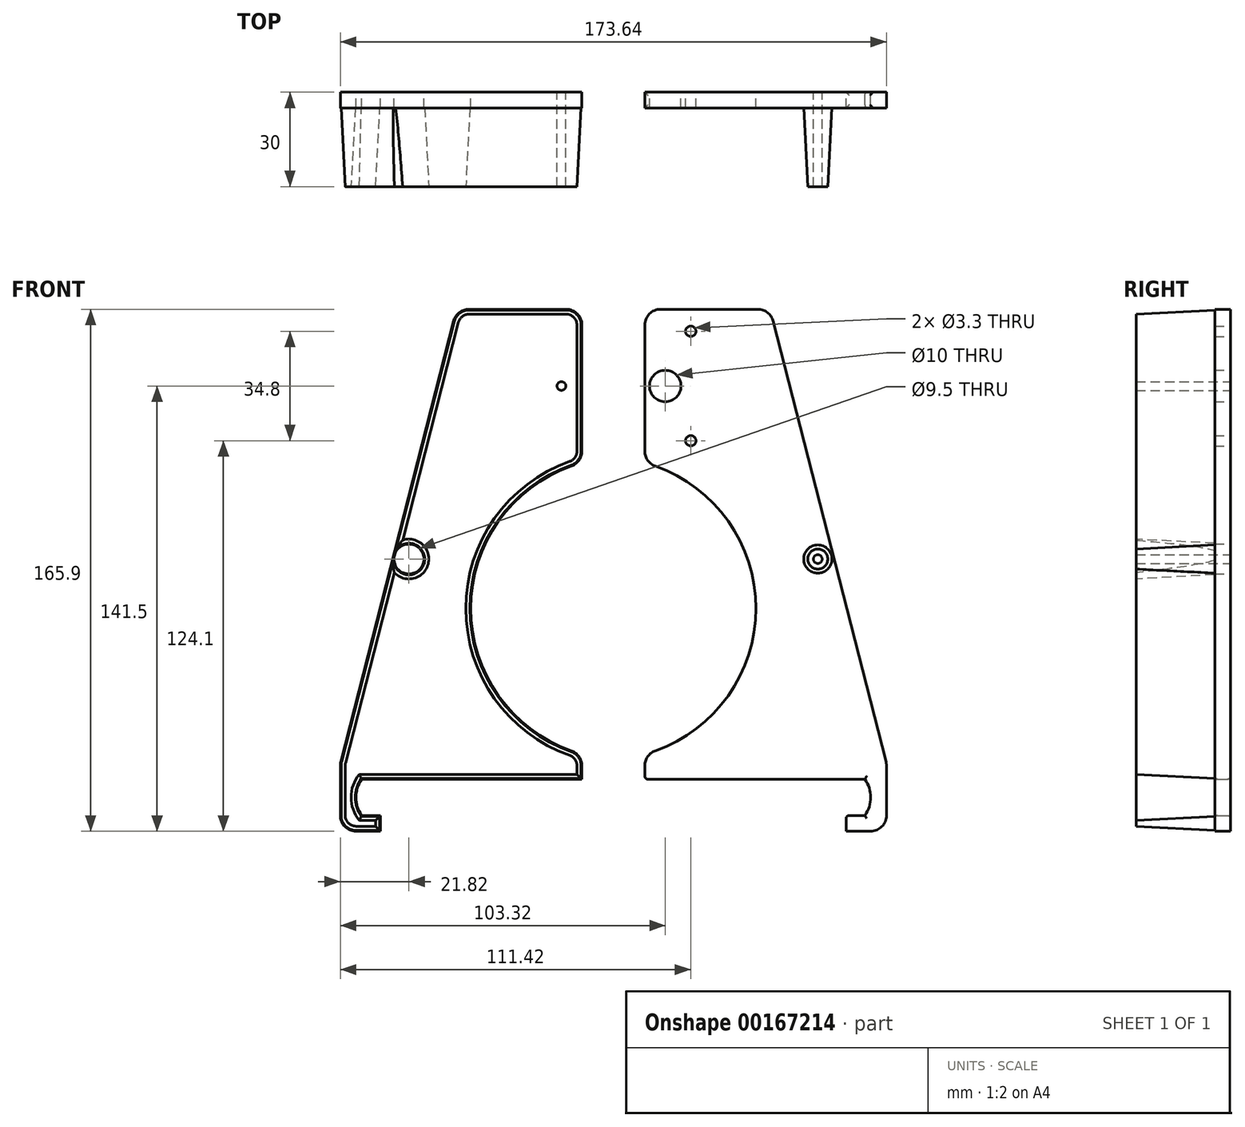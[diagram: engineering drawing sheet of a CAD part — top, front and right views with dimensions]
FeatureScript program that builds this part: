
annotation { "Feature Type Name" : "Feature", "Feature Type Description" : "" }
export const myFeature = defineFeature(function(context is Context, id is Id, definition is map)
    precondition{}
    {
        {
            var Q0;
            Q0=qCreatedBy(makeId("Front.planeOp"),FACE);
            var sketch = newSketch(context, id + "F0", { "sketchPlane" : qUnion([Q0])});
            skLineSegment(sketch, "E0", {"start": v(0, 0) * mm, "end": v(70, 0) * mm});
            skLineSegment(sketch, "E1", {"start": v(70, -11.5) * mm, "end": v(64, -11.5) * mm});
            skLineSegment(sketch, "E2", {"start": v(64, -11.5) * mm, "end": v(64, -16.5) * mm});
            skLineSegment(sketch, "E3", {"start": v(64, -16.5) * mm, "end": v(71.82, -16.5) * mm});
            skLineSegment(sketch, "E4", {"start": v(76.82, -11.5) * mm, "end": v(76.82, 4.37) * mm});
            skLineSegment(sketch, "E5", {"start": v(76.66, 5.61) * mm, "end": v(40.78, 145.64) * mm});
            skLineSegment(sketch, "E6", {"start": v(35.93, 149.4) * mm, "end": v(5, 149.4) * mm});
            skLineSegment(sketch, "E7", {"start": v(0, 144.4) * mm, "end": v(0, 104.27) * mm});
            skArc(sketch, "E8", {"start": v(70, 0) * mm, "mid": v(71.82, -5.75) * mm, "end": v(70, -11.5) * mm});
            skPoint(sketch, "E9", {"position": v(55, 70) * mm});
            skPoint(sketch, "E10", {"position": v(6.5, 125) * mm});
            skPoint(sketch, "E11", {"position": v(14.6, 142.4) * mm});
            skPoint(sketch, "E12", {"position": v(14.6, 107.6) * mm});
            skLineSegment(sketch, "E13", {"start": v(0, 0) * mm, "end": v(0, 4.33) * mm});
            skArc(sketch, "E14", {"start": v(3.33, 9.04) * mm, "mid": v(35.34, 54.3) * mm, "end": v(3.33, 99.56) * mm});
            skCircle(sketch, "E15", {"center": v(55, 70) * mm, "radius": 4.75 * mm});
            skLineSegment(sketch, "E16", {"start": v(-10, 173.2) * mm, "end": v(-10, -16.35) * mm, "construction": true});
            skPoint(sketch, "E17.visualSharp", {"position": v(39.81, 149.4) * mm});
            skArc(sketch, "E17.filletArc", {"start": v(40.78, 145.64) * mm, "mid": v(39, 148.35) * mm, "end": v(35.93, 149.4) * mm});
            skPoint(sketch, "E18.visualSharp", {"position": v(0, 149.4) * mm});
            skArc(sketch, "E18.filletArc", {"start": v(5, 149.4) * mm, "mid": v(1.46, 147.94) * mm, "end": v(0, 144.4) * mm});
            skPoint(sketch, "E19.visualSharp", {"position": v(0, 100.6) * mm});
            skArc(sketch, "E19.filletArc", {"start": v(0, 104.27) * mm, "mid": v(0.92, 101.38) * mm, "end": v(3.33, 99.56) * mm});
            skPoint(sketch, "E20.visualSharp", {"position": v(0, 8) * mm});
            skArc(sketch, "E20.filletArc", {"start": v(3.33, 9.04) * mm, "mid": v(0.92, 7.22) * mm, "end": v(0, 4.33) * mm});
            skPoint(sketch, "E21.visualSharp", {"position": v(76.82, -16.5) * mm});
            skArc(sketch, "E21.filletArc", {"start": v(71.82, -16.5) * mm, "mid": v(75.35, -15.04) * mm, "end": v(76.82, -11.5) * mm});
            skPoint(sketch, "E22.visualSharp", {"position": v(76.82, 5) * mm});
            skArc(sketch, "E22.filletArc", {"start": v(76.82, 4.37) * mm, "mid": v(76.78, 5) * mm, "end": v(76.66, 5.61) * mm});
            skLineSegment(sketch, "E23.MirrorCS", {"start": v(-20, 144.4) * mm, "end": v(-20, 104.27) * mm});
            skPoint(sketch, "E24.MirrorP", {"position": v(-96.82, 5) * mm});
            skLineSegment(sketch, "E25.MirrorCS", {"start": v(-96.82, -11.5) * mm, "end": v(-96.82, 4.37) * mm});
            skLineSegment(sketch, "E26.MirrorCS", {"start": v(-84, -16.5) * mm, "end": v(-91.82, -16.5) * mm});
            skPoint(sketch, "E27.MirrorP", {"position": v(-20, 100.6) * mm});
            skLineSegment(sketch, "E28.MirrorCS", {"start": v(-84, -11.5) * mm, "end": v(-84, -16.5) * mm});
            skPoint(sketch, "E29.MirrorP", {"position": v(-59.81, 149.4) * mm});
            skPoint(sketch, "E30.MirrorP", {"position": v(-34.6, 142.4) * mm});
            skLineSegment(sketch, "E31.MirrorCS", {"start": v(-90, -11.5) * mm, "end": v(-84, -11.5) * mm});
            skArc(sketch, "E32.MirrorCS", {"start": v(-23.33, 9.04) * mm, "mid": v(-20.92, 7.22) * mm, "end": v(-20, 4.33) * mm});
            skPoint(sketch, "E33.MirrorP", {"position": v(-96.82, -16.5) * mm});
            skCircle(sketch, "E34.MirrorC", {"center": v(-75, 70) * mm, "radius": 4.75 * mm});
            skLineSegment(sketch, "E35.MirrorCS", {"start": v(-20, 0) * mm, "end": v(-90, 0) * mm});
            skArc(sketch, "E36.MirrorCS", {"start": v(-20, 104.27) * mm, "mid": v(-20.92, 101.38) * mm, "end": v(-23.33, 99.56) * mm});
            skPoint(sketch, "E37.MirrorP", {"position": v(-34.6, 107.6) * mm});
            skArc(sketch, "E38.MirrorCS", {"start": v(-23.33, 9.04) * mm, "mid": v(-55.34, 54.3) * mm, "end": v(-23.33, 99.56) * mm});
            skArc(sketch, "E39.MirrorCS", {"start": v(-25, 149.4) * mm, "mid": v(-21.46, 147.94) * mm, "end": v(-20, 144.4) * mm});
            skArc(sketch, "E40.MirrorCS", {"start": v(-91.82, -16.5) * mm, "mid": v(-95.35, -15.04) * mm, "end": v(-96.82, -11.5) * mm});
            skLineSegment(sketch, "E41.MirrorCS", {"start": v(-20, 0) * mm, "end": v(-20, 4.33) * mm});
            skPoint(sketch, "E42.MirrorP", {"position": v(-20, 149.4) * mm});
            skArc(sketch, "E43.MirrorCS", {"start": v(-60.78, 145.64) * mm, "mid": v(-59, 148.35) * mm, "end": v(-55.93, 149.4) * mm});
            skLineSegment(sketch, "E44.MirrorCS", {"start": v(-55.93, 149.4) * mm, "end": v(-25, 149.4) * mm});
            skPoint(sketch, "E45.MirrorP", {"position": v(-26.5, 125) * mm});
            skArc(sketch, "E46.MirrorCS", {"start": v(-90, 0) * mm, "mid": v(-91.82, -5.75) * mm, "end": v(-90, -11.5) * mm});
            skLineSegment(sketch, "E47.MirrorCS", {"start": v(-96.66, 5.61) * mm, "end": v(-60.78, 145.64) * mm});
            skArc(sketch, "E48.MirrorCS", {"start": v(-96.82, 4.37) * mm, "mid": v(-96.78, 5) * mm, "end": v(-96.66, 5.61) * mm});
            skPoint(sketch, "E49.MirrorP", {"position": v(-20, 8) * mm});
            skSolve(sketch);
        }
        {
            var Q0;
            Q0=makeQuery(id+"F0.imprint","IMPRINT",FACE,{"disambiguationData":[TD([[makeQuery(id+"F0.imprint","IMPRINT",EDGE,{"derivedFrom":sQuery(id+"F0.wireOp",EDGE,"E0")}),1.0]])]});
            var Q1;
            Q1=makeQuery(id+"F0.imprint","IMPRINT",FACE,{"disambiguationData":[TD([[makeQuery(id+"F0.imprint","IMPRINT",EDGE,{"derivedFrom":sQuery(id+"F0.wireOp",EDGE,"E23.MirrorCS")}),-1.0]])]});
            var Q2;
            Q2=makeQuery(id+"F0.imprint","IMPRINT",FACE,{"disambiguationData":[TD([[makeQuery(id+"F0.imprint","IMPRINT",EDGE,{"derivedFrom":sQuery(id+"F0.wireOp",EDGE,"E15")}),1.0]])]});
            var Q3;
            Q3=makeQuery(id+"F0.imprint","IMPRINT",FACE,{"disambiguationData":[TD([[makeQuery(id+"F0.imprint","IMPRINT",EDGE,{"derivedFrom":sQuery(id+"F0.wireOp",EDGE,"E34.MirrorC")}),-1.0]])]});
            extrude(context, id + "F1", {"entities" : qUnion([Q0, Q1, Q2, Q3]), "depth" : 5 * mm});
        }
        {
            var Q0;
            Q0=makeQuery(id+"F0.imprint","IMPRINT",FACE,{"disambiguationData":[TD([[makeQuery(id+"F0.imprint","IMPRINT",EDGE,{"derivedFrom":sQuery(id+"F0.wireOp",EDGE,"E15")}),1.0]])]});
            var Q1;
            Q1=makeQuery(id+"F0.imprint","IMPRINT",FACE,{"disambiguationData":[TD([[makeQuery(id+"F0.imprint","IMPRINT",EDGE,{"derivedFrom":sQuery(id+"F0.wireOp",EDGE,"E34.MirrorC")}),-1.0]])]});
            extrude(context, id + "F2", {"entities" : qUnion([Q0, Q1]), "operationType" : NewBodyOperationType.ADD, "depth" : 30 * mm, "hasDraft" : true, "draftAngle" : 3 * degree, "draftPullDirection" : true});
        }
        {
            var Q0;
            Q0=sQuery(id+"F0.wireOp",VERTEX,"E11");
            var Q1;
            Q1=sQuery(id+"F0.wireOp",VERTEX,"E12");
            var Q2;
            Q2=makeQuery(id+"F1.opExtrude","SWEPT_BODY",BODY,{"disambiguationData":[OSD([sQuery(id+"F0.wireOp",EDGE,"E23.MirrorCS"),sQuery(id+"F0.wireOp",EDGE,"E25.MirrorCS"),sQuery(id+"F0.wireOp",EDGE,"E26.MirrorCS"),sQuery(id+"F0.wireOp",EDGE,"E28.MirrorCS"),sQuery(id+"F0.wireOp",EDGE,"E31.MirrorCS"),sQuery(id+"F0.wireOp",EDGE,"E32.MirrorCS"),sQuery(id+"F0.wireOp",EDGE,"E34.MirrorC"),sQuery(id+"F0.wireOp",EDGE,"E35.MirrorCS"),sQuery(id+"F0.wireOp",EDGE,"E36.MirrorCS"),sQuery(id+"F0.wireOp",EDGE,"E38.MirrorCS"),sQuery(id+"F0.wireOp",EDGE,"E39.MirrorCS"),sQuery(id+"F0.wireOp",EDGE,"E40.MirrorCS"),sQuery(id+"F0.wireOp",EDGE,"E41.MirrorCS"),sQuery(id+"F0.wireOp",EDGE,"E43.MirrorCS"),sQuery(id+"F0.wireOp",EDGE,"E44.MirrorCS"),sQuery(id+"F0.wireOp",EDGE,"E46.MirrorCS"),sQuery(id+"F0.wireOp",EDGE,"E47.MirrorCS"),sQuery(id+"F0.wireOp",EDGE,"E48.MirrorCS")])]});
            var Q3;
            Q3=makeQuery(id+"F1.opExtrude","SWEPT_BODY",BODY,{"disambiguationData":[OSD([sQuery(id+"F0.wireOp",EDGE,"E0"),sQuery(id+"F0.wireOp",EDGE,"E1"),sQuery(id+"F0.wireOp",EDGE,"E2"),sQuery(id+"F0.wireOp",EDGE,"E3"),sQuery(id+"F0.wireOp",EDGE,"E4"),sQuery(id+"F0.wireOp",EDGE,"E5"),sQuery(id+"F0.wireOp",EDGE,"E6"),sQuery(id+"F0.wireOp",EDGE,"E7"),sQuery(id+"F0.wireOp",EDGE,"E8"),sQuery(id+"F0.wireOp",EDGE,"E13"),sQuery(id+"F0.wireOp",EDGE,"E14"),sQuery(id+"F0.wireOp",EDGE,"E15"),sQuery(id+"F0.wireOp",EDGE,"E17.filletArc"),sQuery(id+"F0.wireOp",EDGE,"E18.filletArc"),sQuery(id+"F0.wireOp",EDGE,"E19.filletArc"),sQuery(id+"F0.wireOp",EDGE,"E20.filletArc"),sQuery(id+"F0.wireOp",EDGE,"E21.filletArc"),sQuery(id+"F0.wireOp",EDGE,"E22.filletArc")])]});
            hole(context, id + "F3", {"style" : HoleStyle.SIMPLE, "endStyle" : HoleEndStyle.THROUGH, "oppositeDirection" : true, "standardTappedOrClearance" : lookupTablePath({ "standard" : "ISO", "fit" : "Normal", "size" : "M3", "type" : "Clearance" }), "standardBlindInLast" : lookupTablePath({ "fit" : "Standard", "standard" : "ISO", "size" : "M3", "type" : "Clearance" }), "holeDiameter" : 3.3 * mm, "locations" : qUnion([Q0, Q1]), "scope" : qUnion([Q2, Q3]), "isTappedThrough" : true});
        }
        {
            var Q0;
            Q0=sQuery(id+"F0.wireOp",VERTEX,"E34.MirrorC.center");
            var Q1;
            Q1=sQuery(id+"F0.wireOp",VERTEX,"E45.MirrorP");
            var Q2;
            Q2=sQuery(id+"F0.wireOp",VERTEX,"E9");
            var Q3;
            Q3=makeQuery(id+"F1.opExtrude","SWEPT_BODY",BODY,{"disambiguationData":[OSD([sQuery(id+"F0.wireOp",EDGE,"E23.MirrorCS"),sQuery(id+"F0.wireOp",EDGE,"E25.MirrorCS"),sQuery(id+"F0.wireOp",EDGE,"E26.MirrorCS"),sQuery(id+"F0.wireOp",EDGE,"E28.MirrorCS"),sQuery(id+"F0.wireOp",EDGE,"E31.MirrorCS"),sQuery(id+"F0.wireOp",EDGE,"E32.MirrorCS"),sQuery(id+"F0.wireOp",EDGE,"E34.MirrorC"),sQuery(id+"F0.wireOp",EDGE,"E35.MirrorCS"),sQuery(id+"F0.wireOp",EDGE,"E36.MirrorCS"),sQuery(id+"F0.wireOp",EDGE,"E38.MirrorCS"),sQuery(id+"F0.wireOp",EDGE,"E39.MirrorCS"),sQuery(id+"F0.wireOp",EDGE,"E40.MirrorCS"),sQuery(id+"F0.wireOp",EDGE,"E41.MirrorCS"),sQuery(id+"F0.wireOp",EDGE,"E43.MirrorCS"),sQuery(id+"F0.wireOp",EDGE,"E44.MirrorCS"),sQuery(id+"F0.wireOp",EDGE,"E46.MirrorCS"),sQuery(id+"F0.wireOp",EDGE,"E47.MirrorCS"),sQuery(id+"F0.wireOp",EDGE,"E48.MirrorCS")])]});
            var Q4;
            Q4=makeQuery(id+"F1.opExtrude","SWEPT_BODY",BODY,{"disambiguationData":[OSD([sQuery(id+"F0.wireOp",EDGE,"E0"),sQuery(id+"F0.wireOp",EDGE,"E1"),sQuery(id+"F0.wireOp",EDGE,"E2"),sQuery(id+"F0.wireOp",EDGE,"E3"),sQuery(id+"F0.wireOp",EDGE,"E4"),sQuery(id+"F0.wireOp",EDGE,"E5"),sQuery(id+"F0.wireOp",EDGE,"E6"),sQuery(id+"F0.wireOp",EDGE,"E7"),sQuery(id+"F0.wireOp",EDGE,"E8"),sQuery(id+"F0.wireOp",EDGE,"E13"),sQuery(id+"F0.wireOp",EDGE,"E14"),sQuery(id+"F0.wireOp",EDGE,"E15"),sQuery(id+"F0.wireOp",EDGE,"E17.filletArc"),sQuery(id+"F0.wireOp",EDGE,"E18.filletArc"),sQuery(id+"F0.wireOp",EDGE,"E19.filletArc"),sQuery(id+"F0.wireOp",EDGE,"E20.filletArc"),sQuery(id+"F0.wireOp",EDGE,"E21.filletArc"),sQuery(id+"F0.wireOp",EDGE,"E22.filletArc")])]});
            hole(context, id + "F4", {"style" : HoleStyle.SIMPLE, "endStyle" : HoleEndStyle.THROUGH, "oppositeDirection" : true, "holeDiameter" : 2.8 * mm, "locations" : qUnion([Q0, Q1, Q2]), "scope" : qUnion([Q3, Q4]), "isTappedThrough" : true});
        }
        {
            var Q0;
            Q0=sQuery(id+"F0.wireOp",VERTEX,"E10");
            var Q1;
            Q1=makeQuery(id+"F1.opExtrude","SWEPT_BODY",BODY,{"disambiguationData":[OSD([sQuery(id+"F0.wireOp",EDGE,"E0"),sQuery(id+"F0.wireOp",EDGE,"E1"),sQuery(id+"F0.wireOp",EDGE,"E2"),sQuery(id+"F0.wireOp",EDGE,"E3"),sQuery(id+"F0.wireOp",EDGE,"E4"),sQuery(id+"F0.wireOp",EDGE,"E5"),sQuery(id+"F0.wireOp",EDGE,"E6"),sQuery(id+"F0.wireOp",EDGE,"E7"),sQuery(id+"F0.wireOp",EDGE,"E8"),sQuery(id+"F0.wireOp",EDGE,"E13"),sQuery(id+"F0.wireOp",EDGE,"E14"),sQuery(id+"F0.wireOp",EDGE,"E15"),sQuery(id+"F0.wireOp",EDGE,"E17.filletArc"),sQuery(id+"F0.wireOp",EDGE,"E18.filletArc"),sQuery(id+"F0.wireOp",EDGE,"E19.filletArc"),sQuery(id+"F0.wireOp",EDGE,"E20.filletArc"),sQuery(id+"F0.wireOp",EDGE,"E21.filletArc"),sQuery(id+"F0.wireOp",EDGE,"E22.filletArc")])]});
            hole(context, id + "F5", {"style" : HoleStyle.SIMPLE, "endStyle" : HoleEndStyle.THROUGH, "oppositeDirection" : true, "holeDiameter" : 10 * mm, "locations" : qUnion([Q0]), "scope" : qUnion([Q1]), "isTappedThrough" : true});
        }
        {
            var Q0;
            Q0=makeQuery(id+"F1.opExtrude","CAP_EDGE",EDGE,{"disambiguationData":[OSD([sQuery(id+"F0.wireOp",EDGE,"E35.MirrorCS")])],"isStart":true});
            var Q1;
            Q1=makeQuery(id+"F1.opExtrude","CAP_EDGE",EDGE,{"disambiguationData":[OSD([sQuery(id+"F0.wireOp",EDGE,"E35.MirrorCS")])],"isStart":false});
            var Q2;
            Q2=makeQuery(id+"F1.opExtrude","SWEPT_EDGE",EDGE,{"disambiguationData":[OSD([sQuery(id+"F0.wireOp",EDGE,"E35.MirrorCS"),sQuery(id+"F0.wireOp",EDGE,"E41.MirrorCS")])]});
            var Q3;
            Q3=makeQuery(id+"F1.opExtrude","CAP_EDGE",EDGE,{"disambiguationData":[OSD([sQuery(id+"F0.wireOp",EDGE,"E46.MirrorCS")])],"isStart":false});
            var Q4;
            Q4=makeQuery(id+"F1.opExtrude","CAP_EDGE",EDGE,{"disambiguationData":[OSD([sQuery(id+"F0.wireOp",EDGE,"E46.MirrorCS")])],"isStart":true});
            var Q5;
            Q5=makeQuery(id+"F1.opExtrude","CAP_EDGE",EDGE,{"disambiguationData":[OSD([sQuery(id+"F0.wireOp",EDGE,"E31.MirrorCS")])],"isStart":true});
            var Q6;
            Q6=makeQuery(id+"F1.opExtrude","CAP_EDGE",EDGE,{"disambiguationData":[OSD([sQuery(id+"F0.wireOp",EDGE,"E31.MirrorCS")])],"isStart":false});
            var Q7;
            Q7=makeQuery(id+"F1.opExtrude","SWEPT_EDGE",EDGE,{"disambiguationData":[OSD([sQuery(id+"F0.wireOp",EDGE,"E28.MirrorCS"),sQuery(id+"F0.wireOp",EDGE,"E31.MirrorCS")])]});
            var Q8;
            Q8=makeQuery(id+"F1.opExtrude","SWEPT_EDGE",EDGE,{"disambiguationData":[OSD([sQuery(id+"F0.wireOp",EDGE,"E0"),sQuery(id+"F0.wireOp",EDGE,"E13")])]});
            var Q9;
            Q9=makeQuery(id+"F1.opExtrude","CAP_EDGE",EDGE,{"disambiguationData":[OSD([sQuery(id+"F0.wireOp",EDGE,"E0")])],"isStart":false});
            var Q10;
            Q10=makeQuery(id+"F1.opExtrude","CAP_EDGE",EDGE,{"disambiguationData":[OSD([sQuery(id+"F0.wireOp",EDGE,"E0")])],"isStart":true});
            var Q11;
            Q11=makeQuery(id+"F1.opExtrude","CAP_EDGE",EDGE,{"disambiguationData":[OSD([sQuery(id+"F0.wireOp",EDGE,"E8")])],"isStart":true});
            var Q12;
            Q12=makeQuery(id+"F1.opExtrude","CAP_EDGE",EDGE,{"disambiguationData":[OSD([sQuery(id+"F0.wireOp",EDGE,"E8")])],"isStart":false});
            var Q13;
            Q13=makeQuery(id+"F1.opExtrude","CAP_EDGE",EDGE,{"disambiguationData":[OSD([sQuery(id+"F0.wireOp",EDGE,"E1")])],"isStart":false});
            var Q14;
            Q14=makeQuery(id+"F1.opExtrude","CAP_EDGE",EDGE,{"disambiguationData":[OSD([sQuery(id+"F0.wireOp",EDGE,"E1")])],"isStart":true});
            var Q15;
            Q15=makeQuery(id+"F1.opExtrude","SWEPT_EDGE",EDGE,{"disambiguationData":[OSD([sQuery(id+"F0.wireOp",EDGE,"E1"),sQuery(id+"F0.wireOp",EDGE,"E2")])]});
            fillet(context, id + "F6", {"entities" : qUnion([Q0, Q1, Q2, Q3, Q4, Q5, Q6, Q7, Q8, Q9, Q10, Q11, Q12, Q13, Q14, Q15]), "radius" : 1 * mm, "tangentPropagation" : true, "allowEdgeOverflow" : false});
        }
    });
